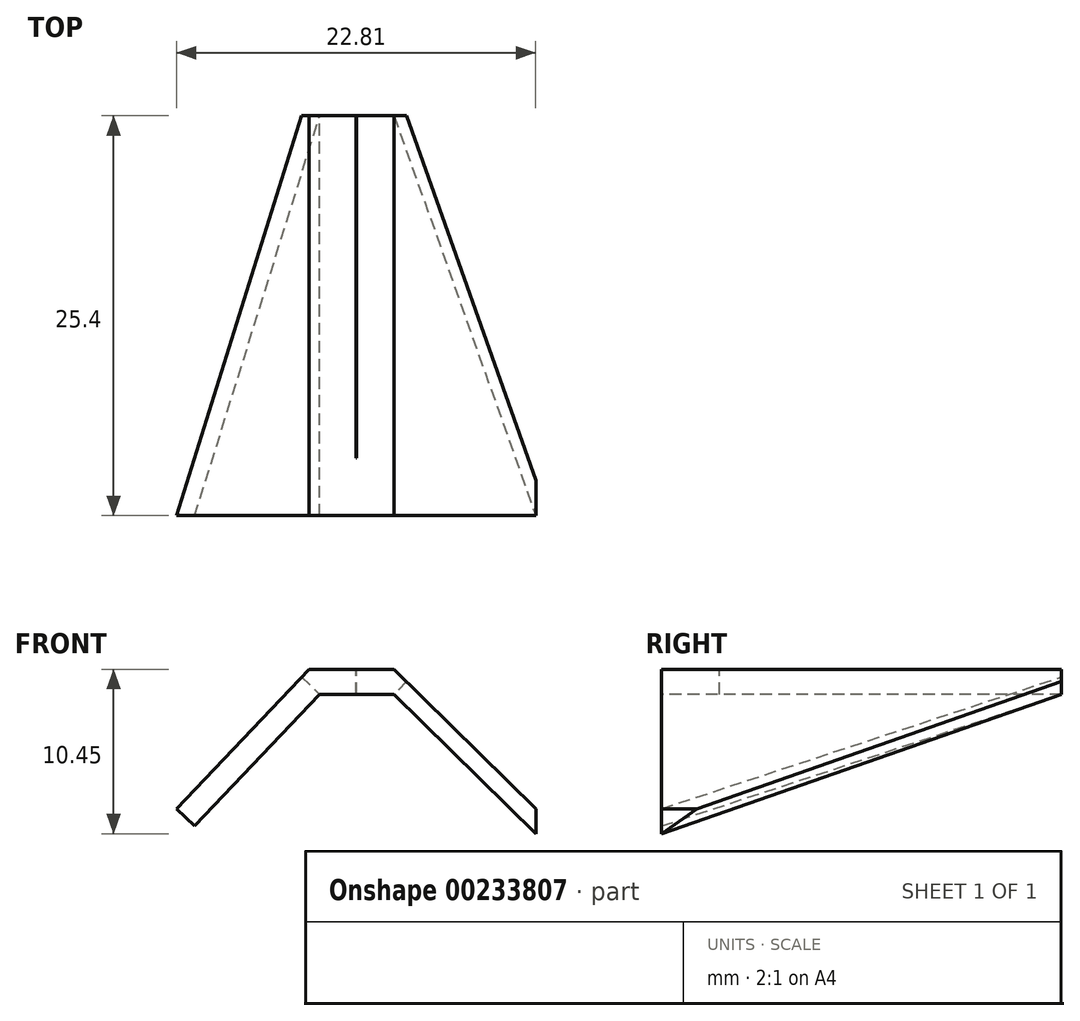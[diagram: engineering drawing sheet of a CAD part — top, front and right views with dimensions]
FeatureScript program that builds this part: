
annotation { "Feature Type Name" : "Feature", "Feature Type Description" : "" }
export const myFeature = defineFeature(function(context is Context, id is Id, definition is map)
    precondition{}
    {
        {
            var Q0;
            Q0=qCreatedBy(makeId("Front.planeOp"),FACE);
            var sketch = newSketch(context, id + "F0", { "sketchPlane" : qUnion([Q0])});
            skLineSegment(sketch, "E0", {"start": v(-11.4, 0) * mm, "end": v(-3, 8.86) * mm});
            skLineSegment(sketch, "E1", {"start": v(-3, 8.86) * mm, "end": v(2.4, 8.86) * mm});
            skLineSegment(sketch, "E2", {"start": v(2.4, 8.86) * mm, "end": v(11.4, 0) * mm});
            skSolve(sketch);
        }
        {
            var Q0;
            Q0=sQuery(id+"F0.wireOp",EDGE,"E0");
            var Q1;
            Q1=sQuery(id+"F0.wireOp",EDGE,"E1");
            var Q2;
            Q2=sQuery(id+"F0.wireOp",EDGE,"E2");
            extrude(context, id + "F1", {"bodyType" : ToolBodyType.SURFACE, "surfaceEntities" : qUnion([Q0, Q1, Q2]), "depth" : 25.4 * mm});
        }
        {
            var Q0;
            Q0=makeQuery(id+"F1.opExtrude","SWEPT_FACE",FACE,{"disambiguationData":[OSD([sQuery(id+"F0.wireOp",EDGE,"E0")])]});
            extrude(context, id + "F2", {"entities" : qUnion([Q0]), "depth" : 1.59 * mm});
        }
        {
            var Q0;
            Q0=makeQuery(id+"F1.opExtrude","SWEPT_FACE",FACE,{"disambiguationData":[OSD([sQuery(id+"F0.wireOp",EDGE,"E1")])]});
            var Q1;
            Q1=makeQuery(id+"F1.opExtrude","SWEPT_FACE",FACE,{"disambiguationData":[OSD([sQuery(id+"F0.wireOp",EDGE,"E2")])]});
            extrude(context, id + "F3", {"entities" : qUnion([Q0, Q1]), "operationType" : NewBodyOperationType.ADD, "depth" : 1.59 * mm});
        }
        {
            var Q0;
            Q0=makeQuery(id+"F2.opExtrude","CAP_FACE",FACE,{"disambiguationData":[OSD([sQuery(id+"F0.wireOp",EDGE,"E0")])],"isStart":false});
            var sketch = newSketch(context, id + "F4", { "sketchPlane" : qUnion([Q0])});
            skLineSegment(sketch, "E3", {"start": v(-25.4, -7.85) * mm, "end": v(0, 3.67) * mm});
            skLineSegment(sketch, "E4", {"start": v(0, 3.67) * mm, "end": v(0, -7.85) * mm});
            skLineSegment(sketch, "E5", {"start": v(0, -7.85) * mm, "end": v(-25.4, -7.85) * mm});
            skSolve(sketch);
        }
        {
            var Q0;
            Q0 = qSketchRegion(id + "F4", true);
            extrude(context, id + "F5", {"entities" : qUnion([Q0]), "operationType" : NewBodyOperationType.REMOVE, "oppositeDirection" : true, "depth" : 6.35 * mm});
        }
        {
            var Q0;
            Q0=makeQuery(id+"F3.opExtrude","CAP_FACE",FACE,{"disambiguationData":[OSD([sQuery(id+"F0.wireOp",EDGE,"E2")]),OD(0.0)],"isStart":false});
            var sketch = newSketch(context, id + "F6", { "sketchPlane" : qUnion([Q0])});
            skLineSegment(sketch, "E6", {"start": v(-3.39, 0) * mm, "end": v(9.24, 25.4) * mm});
            skLineSegment(sketch, "E7", {"start": v(9.24, 25.4) * mm, "end": v(9.24, 0) * mm});
            skLineSegment(sketch, "E8", {"start": v(9.24, 0) * mm, "end": v(-3.39, 0) * mm});
            skSolve(sketch);
        }
        {
            var Q0;
            Q0 = qSketchRegion(id + "F6", true);
            extrude(context, id + "F7", {"entities" : qUnion([Q0]), "operationType" : NewBodyOperationType.REMOVE, "oppositeDirection" : true, "depth" : 25.4 * mm});
        }
        {
            var Q0;
            Q0=makeQuery(id+"F1.opExtrude","SWEPT_FACE",FACE,{"disambiguationData":[OSD([sQuery(id+"F0.wireOp",EDGE,"E1")])]});
            var sketch = newSketch(context, id + "F8", { "sketchPlane" : qUnion([Q0])});
            skLineSegment(sketch, "E9", {"start": v(-0.02, 21.73) * mm, "end": v(-0.02, 0) * mm});
            skLineSegment(sketch, "E10", {"start": v(-0.02, 0) * mm, "end": v(0.02, 0) * mm});
            skLineSegment(sketch, "E11", {"start": v(-0.02, 21.73) * mm, "end": v(0.02, 21.73) * mm});
            skLineSegment(sketch, "E12", {"start": v(0.02, 0) * mm, "end": v(0.02, 21.73) * mm});
            skSolve(sketch);
        }
        {
            var Q0;
            Q0 = qSketchRegion(id + "F8", true);
            extrude(context, id + "F9", {"entities" : qUnion([Q0]), "operationType" : NewBodyOperationType.REMOVE, "depth" : 3.68 * mm});
        }
    });
